FCSTD DOCUMENT  (FreeCAD 0.15R4671 (Git))
Label: tqfp_pin_size
License: All rights reserved
LicenseURL: http://en.wikipedia.org/wiki/All_rights_reserved
objects: Sketcher::SketchObject×1
note: 1 computed .brp shape members not serialized (recipe doc carries the construction recipe); baked Part::Feature solids carry a one-line shape summary decoded from their .brp

FEATURE [Sketcher::SketchObject] Sketch
  sketch-geometry (8):
    g0: LineSegment StartX=0 StartY=40 StartZ=0 EndX=-10 EndY=50 EndZ=0
    g1: LineSegment StartX=-10 StartY=50 StartZ=0 EndX=-39.1949 EndY=50 EndZ=0
    g2: LineSegment StartX=-39.1949 StartY=50 StartZ=0 EndX=-60 EndY=10 EndZ=0
    g3: LineSegment StartX=-60 StartY=10 StartZ=0 EndX=-90 EndY=10 EndZ=0
    g4: LineSegment StartX=-90 StartY=0 StartZ=0 EndX=-50 EndY=0 EndZ=0
    g5: LineSegment StartX=-50 StartY=0 StartZ=0 EndX=-30 EndY=40 EndZ=0
    g6: LineSegment StartX=-30 StartY=40 StartZ=0 EndX=0 EndY=40 EndZ=0
    g7: LineSegment StartX=-90 StartY=10 StartZ=0 EndX=-90 EndY=0 EndZ=0
  constraints (11):
    c: Coincident(g0,g1)
    c: Horizontal(g1)
    c: Coincident(g1,g2)
    c: Coincident(g2,g3)
    c: Horizontal(g3)
    c: Horizontal(g4)
    c: Coincident(g4,g5)
    c: Coincident(g5,g6)
    c: Horizontal(g6)
    c: Coincident(g7,g4)
    c: Vertical(g7)
